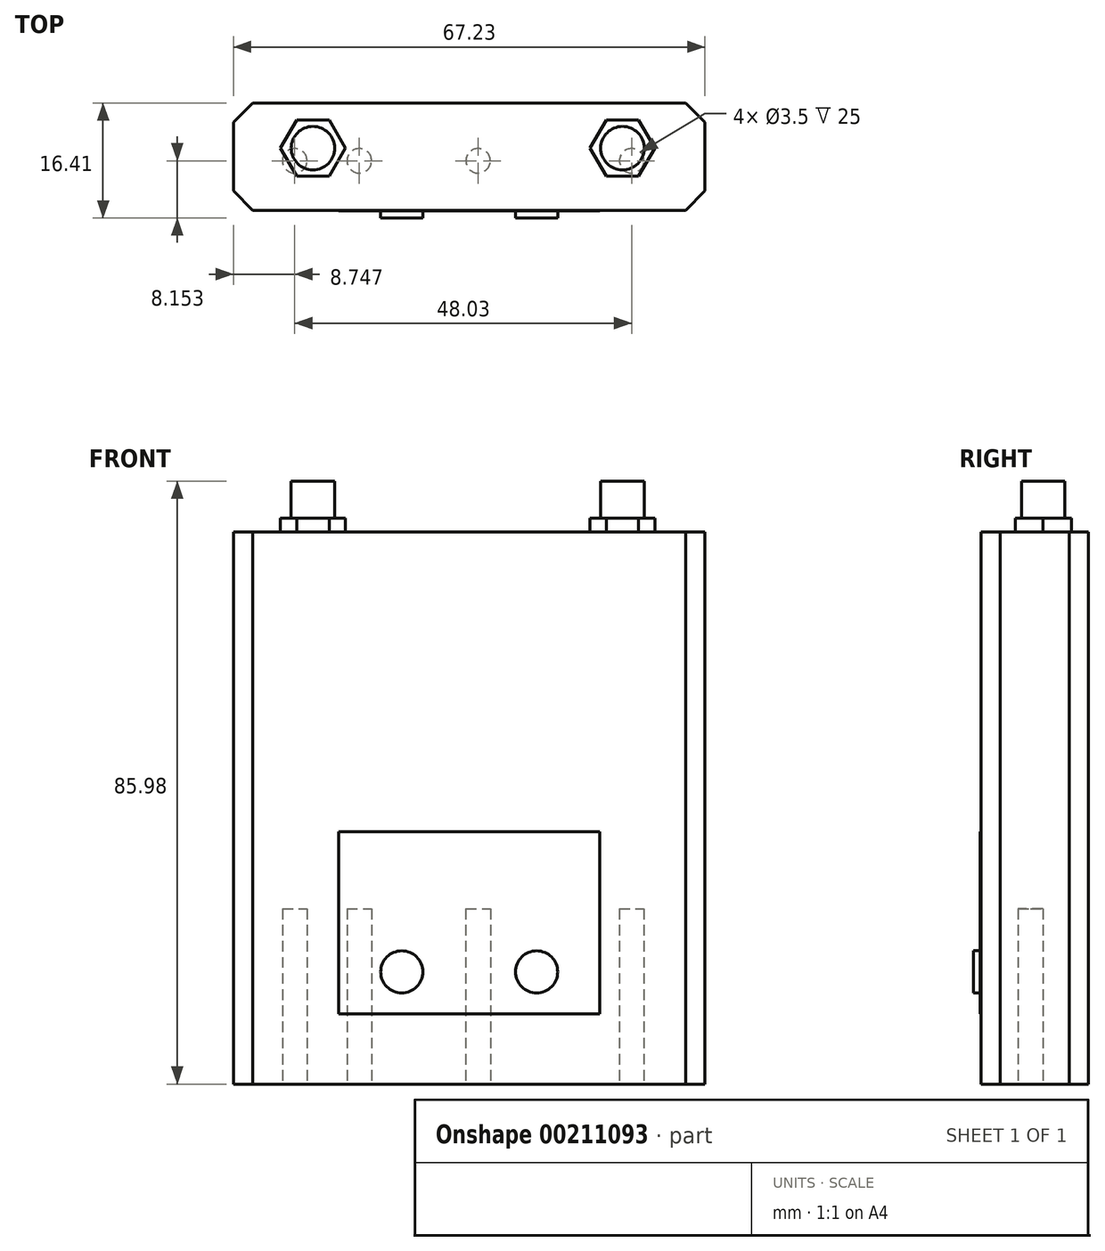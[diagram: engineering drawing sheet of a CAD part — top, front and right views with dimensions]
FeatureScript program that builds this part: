
annotation { "Feature Type Name" : "Feature", "Feature Type Description" : "" }
export const myFeature = defineFeature(function(context is Context, id is Id, definition is map)
    precondition{}
    {
        {
            var Q0;
            Q0=qCreatedBy(makeId("Top.planeOp"),FACE);
            var sketch = newSketch(context, id + "F0", { "sketchPlane" : qUnion([Q0])});
            skLineSegment(sketch, "E0.bottom", {"start": v(-31.85, 6.63) * mm, "end": v(35.38, 6.63) * mm});
            skLineSegment(sketch, "E0.top", {"start": v(-31.85, -8.68) * mm, "end": v(35.38, -8.68) * mm});
            skLineSegment(sketch, "E0.left", {"start": v(-31.85, 6.63) * mm, "end": v(-31.85, -8.68) * mm});
            skLineSegment(sketch, "E0.right", {"start": v(35.38, 6.63) * mm, "end": v(35.38, -8.68) * mm});
            skSolve(sketch);
        }
        {
            var Q0;
            Q0=qSketchRegion(id+"F0",true);
            extrude(context, id + "F1", {"entities" : qUnion([Q0]), "depth" : 78.7 * mm});
        }
        {
            var Q0;
            Q0=makeQuery(id+"F1.opExtrude","CAP_FACE",FACE,{"disambiguationData":[OSD([sQuery(id+"F0.wireOp",EDGE,"E0.bottom"),sQuery(id+"F0.wireOp",EDGE,"E0.top"),sQuery(id+"F0.wireOp",EDGE,"E0.left"),sQuery(id+"F0.wireOp",EDGE,"E0.right")])],"isStart":true});
            var sketch = newSketch(context, id + "F2", { "sketchPlane" : qUnion([Q0])});
            skCircle(sketch, "E1", {"center": v(-23.1, 1.63) * mm, "radius": 1.75 * mm});
            skCircle(sketch, "E2", {"center": v(-13.9, 1.63) * mm, "radius": 1.75 * mm});
            skCircle(sketch, "E3", {"center": v(3.03, 1.63) * mm, "radius": 1.75 * mm});
            skCircle(sketch, "E4", {"center": v(24.93, 1.63) * mm, "radius": 1.75 * mm});
            skSolve(sketch);
        }
        {
            var Q0;
            Q0=qSketchRegion(id+"F2",true);
            extrude(context, id + "F3", {"entities" : qUnion([Q0]), "operationType" : NewBodyOperationType.REMOVE, "oppositeDirection" : true, "depth" : 25 * mm});
        }
        {
            var Q0;
            Q0=makeQuery(id+"F1.opExtrude","CAP_FACE",FACE,{"disambiguationData":[OSD([sQuery(id+"F0.wireOp",EDGE,"E0.bottom"),sQuery(id+"F0.wireOp",EDGE,"E0.top"),sQuery(id+"F0.wireOp",EDGE,"E0.left"),sQuery(id+"F0.wireOp",EDGE,"E0.right")])],"isStart":false});
            var sketch = newSketch(context, id + "F4", { "sketchPlane" : qUnion([Q0])});
            skCircle(sketch, "E5.cCircle", {"center": v(23.6, 0.18) * mm, "radius": 4 * mm, "construction": true});
            skLineSegment(sketch, "E5.0", {"start": v(21.3, 4.18) * mm, "end": v(25.92, 4.18) * mm});
            skLineSegment(sketch, "E5.1", {"start": v(25.92, 4.18) * mm, "end": v(28.23, 0.18) * mm});
            skLineSegment(sketch, "E5.2", {"start": v(28.23, 0.18) * mm, "end": v(25.92, -3.82) * mm});
            skLineSegment(sketch, "E5.3", {"start": v(25.92, -3.82) * mm, "end": v(21.3, -3.82) * mm});
            skLineSegment(sketch, "E5.4", {"start": v(21.3, -3.82) * mm, "end": v(18.99, 0.18) * mm});
            skLineSegment(sketch, "E5.5", {"start": v(18.99, 0.18) * mm, "end": v(21.3, 4.18) * mm});
            skPoint(sketch, "E5.0.midPoint", {"position": v(23.6, 4.18) * mm});
            skCircle(sketch, "E6.cCircle", {"center": v(-20.51, 0.18) * mm, "radius": 4 * mm, "construction": true});
            skLineSegment(sketch, "E6.0", {"start": v(-22.82, 4.18) * mm, "end": v(-18.2, 4.18) * mm});
            skLineSegment(sketch, "E6.1", {"start": v(-18.2, 4.18) * mm, "end": v(-15.9, 0.18) * mm});
            skLineSegment(sketch, "E6.2", {"start": v(-15.9, 0.18) * mm, "end": v(-18.2, -3.82) * mm});
            skLineSegment(sketch, "E6.3", {"start": v(-18.2, -3.82) * mm, "end": v(-22.82, -3.82) * mm});
            skLineSegment(sketch, "E6.4", {"start": v(-22.82, -3.82) * mm, "end": v(-25.13, 0.18) * mm});
            skLineSegment(sketch, "E6.5", {"start": v(-25.13, 0.18) * mm, "end": v(-22.82, 4.18) * mm});
            skPoint(sketch, "E6.0.midPoint", {"position": v(-20.51, 4.18) * mm});
            skCircle(sketch, "E7", {"center": v(-20.51, 0.18) * mm, "radius": 3.1 * mm});
            skCircle(sketch, "E8", {"center": v(23.6, 0.18) * mm, "radius": 3.1 * mm});
            skSolve(sketch);
        }
        {
            var Q0;
            Q0=qSketchRegion(id+"F4",true);
            extrude(context, id + "F5", {"entities" : qUnion([Q0]), "operationType" : NewBodyOperationType.ADD, "depth" : 2 * mm});
        }
        {
            var Q0;
            Q0=makeQuery(id+"F5.boolean.opBoolean","SPLIT",FACE,{"disambiguationData":[TD([makeQuery(id+"F5.opExtrude","SWEPT_FACE",FACE,{"disambiguationData":[OSD([sQuery(id+"F4.wireOp",EDGE,"E7")])]})])],"derivedFrom":makeQuery(id+"F1.opExtrude","CAP_FACE",FACE,{"disambiguationData":[OSD([sQuery(id+"F0.wireOp",EDGE,"E0.bottom"),sQuery(id+"F0.wireOp",EDGE,"E0.top"),sQuery(id+"F0.wireOp",EDGE,"E0.left"),sQuery(id+"F0.wireOp",EDGE,"E0.right")])],"isStart":false})});
            var Q1;
            Q1=makeQuery(id+"F5.boolean.opBoolean","SPLIT",FACE,{"disambiguationData":[TD([makeQuery(id+"F5.opExtrude","SWEPT_FACE",FACE,{"disambiguationData":[OSD([sQuery(id+"F4.wireOp",EDGE,"E8")])]})])],"derivedFrom":makeQuery(id+"F1.opExtrude","CAP_FACE",FACE,{"disambiguationData":[OSD([sQuery(id+"F0.wireOp",EDGE,"E0.bottom"),sQuery(id+"F0.wireOp",EDGE,"E0.top"),sQuery(id+"F0.wireOp",EDGE,"E0.left"),sQuery(id+"F0.wireOp",EDGE,"E0.right")])],"isStart":false})});
            extrude(context, id + "F6", {"entities" : qUnion([Q0, Q1]), "operationType" : NewBodyOperationType.ADD, "depth" : 7.28 * mm});
        }
        {
            var Q0;
            Q0=makeQuery(id+"F1.opExtrude","SWEPT_FACE",FACE,{"disambiguationData":[OSD([sQuery(id+"F0.wireOp",EDGE,"E0.top")])]});
            var sketch = newSketch(context, id + "F7", { "sketchPlane" : qUnion([Q0])});
            skLineSegment(sketch, "E9.bottom", {"start": v(-16.85, 36) * mm, "end": v(20.38, 36) * mm});
            skLineSegment(sketch, "E9.top", {"start": v(-16.85, 10) * mm, "end": v(20.38, 10) * mm});
            skLineSegment(sketch, "E9.left", {"start": v(-16.85, 36) * mm, "end": v(-16.85, 10) * mm});
            skLineSegment(sketch, "E9.right", {"start": v(20.38, 36) * mm, "end": v(20.38, 10) * mm});
            skSolve(sketch);
        }
        {
            var Q0;
            Q0=qSketchRegion(id+"F7",true);
            extrude(context, id + "F8", {"entities" : qUnion([Q0]), "operationType" : NewBodyOperationType.ADD, "depth" : .1 * mm});
        }
        {
            var Q0;
            Q0=makeQuery(id+"F8.opExtrude","CAP_FACE",FACE,{"disambiguationData":[OSD([sQuery(id+"F7.wireOp",EDGE,"E9.bottom"),sQuery(id+"F7.wireOp",EDGE,"E9.top"),sQuery(id+"F7.wireOp",EDGE,"E9.left"),sQuery(id+"F7.wireOp",EDGE,"E9.right")])],"isStart":false});
            var sketch = newSketch(context, id + "F9", { "sketchPlane" : qUnion([Q0])});
            skCircle(sketch, "E10", {"center": v(-7.85, 16) * mm, "radius": 3 * mm});
            skCircle(sketch, "E11", {"center": v(11.38, 16) * mm, "radius": 3 * mm});
            skSolve(sketch);
        }
        {
            var Q0;
            Q0=qSketchRegion(id+"F9",true);
            extrude(context, id + "F10", {"entities" : qUnion([Q0]), "operationType" : NewBodyOperationType.ADD, "depth" : 1 * mm});
        }
        {
            var Q0;
            Q0=makeQuery(id+"F1.opExtrude","SWEPT_EDGE",EDGE,{"disambiguationData":[OSD([sQuery(id+"F0.wireOp",EDGE,"E0.top"),sQuery(id+"F0.wireOp",EDGE,"E0.right")])]});
            var Q1;
            Q1=makeQuery(id+"F1.opExtrude","SWEPT_EDGE",EDGE,{"disambiguationData":[OSD([sQuery(id+"F0.wireOp",EDGE,"E0.bottom"),sQuery(id+"F0.wireOp",EDGE,"E0.right")])]});
            var Q2;
            Q2=makeQuery(id+"F1.opExtrude","SWEPT_EDGE",EDGE,{"disambiguationData":[OSD([sQuery(id+"F0.wireOp",EDGE,"E0.bottom"),sQuery(id+"F0.wireOp",EDGE,"E0.left")])]});
            var Q3;
            Q3=makeQuery(id+"F1.opExtrude","SWEPT_EDGE",EDGE,{"disambiguationData":[OSD([sQuery(id+"F0.wireOp",EDGE,"E0.top"),sQuery(id+"F0.wireOp",EDGE,"E0.left")])]});
            chamfer(context, id + "F11", {"entities" : qUnion([Q0, Q1, Q2, Q3]), "width" : 2.75 * mm, "tangentPropagation" : true});
        }
    });
